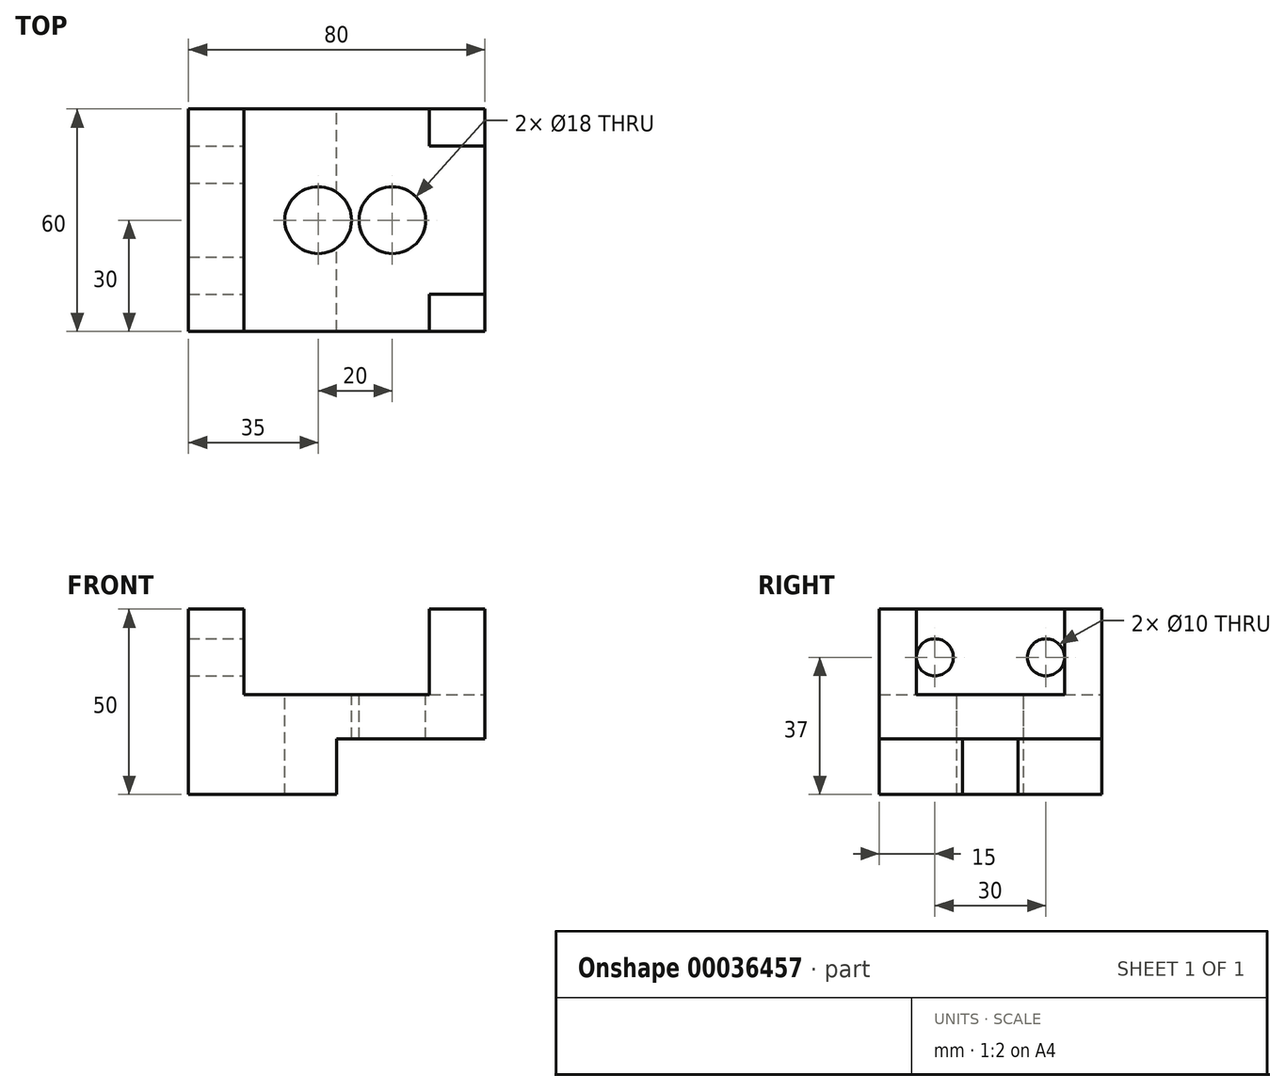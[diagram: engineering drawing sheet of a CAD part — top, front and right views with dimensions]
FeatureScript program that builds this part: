
annotation { "Feature Type Name" : "Feature", "Feature Type Description" : "" }
export const myFeature = defineFeature(function(context is Context, id is Id, definition is map)
    precondition{}
    {
        {
            var Q0;
            Q0=qCreatedBy(makeId("Front.planeOp"),FACE);
            var sketch = newSketch(context, id + "F0", { "sketchPlane" : qUnion([Q0])});
            skLineSegment(sketch, "E0", {"start": v(-40, 35) * mm, "end": v(-40, -15) * mm});
            skLineSegment(sketch, "E1", {"start": v(-40, -15) * mm, "end": v(0, -15) * mm});
            skLineSegment(sketch, "E2", {"start": v(0, -15) * mm, "end": v(0, 0) * mm});
            skLineSegment(sketch, "E3", {"start": v(0, 0) * mm, "end": v(40, 0) * mm});
            skLineSegment(sketch, "E4", {"start": v(40, 0) * mm, "end": v(40, 35) * mm});
            skLineSegment(sketch, "E5", {"start": v(40, 35) * mm, "end": v(25, 35) * mm});
            skLineSegment(sketch, "E6", {"start": v(25, 35) * mm, "end": v(25, 12) * mm});
            skLineSegment(sketch, "E7", {"start": v(25, 12) * mm, "end": v(-25, 12) * mm});
            skLineSegment(sketch, "E8", {"start": v(-25, 12) * mm, "end": v(-25, 35) * mm});
            skLineSegment(sketch, "E9", {"start": v(-25, 35) * mm, "end": v(-40, 35) * mm});
            skSolve(sketch);
        }
        {
            var Q0;
            Q0=makeQuery(id+"F0.imprint","IMPRINT",FACE,{"disambiguationData":[TD([[makeQuery(id+"F0.imprint","IMPRINT",EDGE,{"derivedFrom":sQuery(id+"F0.wireOp",EDGE,"E0")}),1.0]])]});
            extrude(context, id + "F1", {"entities" : qUnion([Q0]), "endBound" : BoundingType.SYMMETRIC, "depth" : 60 * mm});
        }
        {
            var Q0;
            Q0=makeQuery(id+"F1.opExtrude","SWEPT_FACE",FACE,{"disambiguationData":[OSD([sQuery(id+"F0.wireOp",EDGE,"E5")])]});
            var sketch = newSketch(context, id + "F2", { "sketchPlane" : qUnion([Q0])});
            skLineSegment(sketch, "E10.bottom", {"start": v(25, 20) * mm, "end": v(40, 20) * mm});
            skLineSegment(sketch, "E10.top", {"start": v(25, -20) * mm, "end": v(40, -20) * mm});
            skLineSegment(sketch, "E10.left", {"start": v(25, 20) * mm, "end": v(25, -20) * mm});
            skLineSegment(sketch, "E10.right", {"start": v(40, 20) * mm, "end": v(40, -20) * mm});
            skSolve(sketch);
        }
        {
            var Q0;
            Q0 = qSketchRegion(id + "F2", true);
            var Q1;
            Q1=makeQuery(id+"F1.opExtrude","SWEPT_FACE",FACE,{"disambiguationData":[OSD([sQuery(id+"F0.wireOp",EDGE,"E7")])]});
            extrude(context, id + "F3", {"entities" : qUnion([Q0]), "operationType" : NewBodyOperationType.REMOVE, "endBound" : BoundingType.UP_TO_SURFACE, "oppositeDirection" : true, "endBoundEntityFace" : qUnion([Q1]), "depth" : 15 * mm});
        }
        {
            var Q0;
            Q0=makeQuery(id+"F1.opExtrude","SWEPT_FACE",FACE,{"disambiguationData":[OSD([sQuery(id+"F0.wireOp",EDGE,"E8")])]});
            var sketch = newSketch(context, id + "F4", { "sketchPlane" : qUnion([Q0])});
            skCircle(sketch, "E11", {"center": v(-15, 22) * mm, "radius": 5 * mm});
            skCircle(sketch, "E12", {"center": v(15, 22) * mm, "radius": 5 * mm});
            skSolve(sketch);
        }
        {
            var Q0;
            Q0=makeQuery(id+"F4.imprint","IMPRINT",FACE,{"disambiguationData":[TD([[makeQuery(id+"F4.imprint","IMPRINT",EDGE,{"derivedFrom":sQuery(id+"F4.wireOp",EDGE,"E11")}),1.0]])]});
            var Q1;
            Q1=makeQuery(id+"F4.imprint","IMPRINT",FACE,{"disambiguationData":[TD([[makeQuery(id+"F4.imprint","IMPRINT",EDGE,{"derivedFrom":sQuery(id+"F4.wireOp",EDGE,"E12")}),1.0]])]});
            extrude(context, id + "F5", {"entities" : qUnion([Q0, Q1]), "operationType" : NewBodyOperationType.REMOVE, "endBound" : BoundingType.UP_TO_NEXT, "oppositeDirection" : true, "depth" : 25 * mm});
        }
        {
            var Q0;
            Q0=makeQuery(id+"F1.opExtrude","SWEPT_FACE",FACE,{"disambiguationData":[OSD([sQuery(id+"F0.wireOp",EDGE,"E7")])]});
            var sketch = newSketch(context, id + "F6", { "sketchPlane" : qUnion([Q0])});
            skCircle(sketch, "E13", {"center": v(-5, 0) * mm, "radius": 9 * mm});
            skCircle(sketch, "E14", {"center": v(15, 0) * mm, "radius": 9 * mm});
            skSolve(sketch);
        }
        {
            var Q0;
            Q0=makeQuery(id+"F6.imprint","IMPRINT",FACE,{"disambiguationData":[TD([[makeQuery(id+"F6.imprint","IMPRINT",EDGE,{"derivedFrom":sQuery(id+"F6.wireOp",EDGE,"E13")}),1.0]])]});
            var Q1;
            Q1=makeQuery(id+"F6.imprint","IMPRINT",FACE,{"disambiguationData":[TD([[makeQuery(id+"F6.imprint","IMPRINT",EDGE,{"derivedFrom":sQuery(id+"F6.wireOp",EDGE,"E14")}),1.0]])]});
            extrude(context, id + "F7", {"entities" : qUnion([Q0, Q1]), "operationType" : NewBodyOperationType.REMOVE, "endBound" : BoundingType.UP_TO_NEXT, "oppositeDirection" : true, "depth" : 25 * mm});
        }
    });
